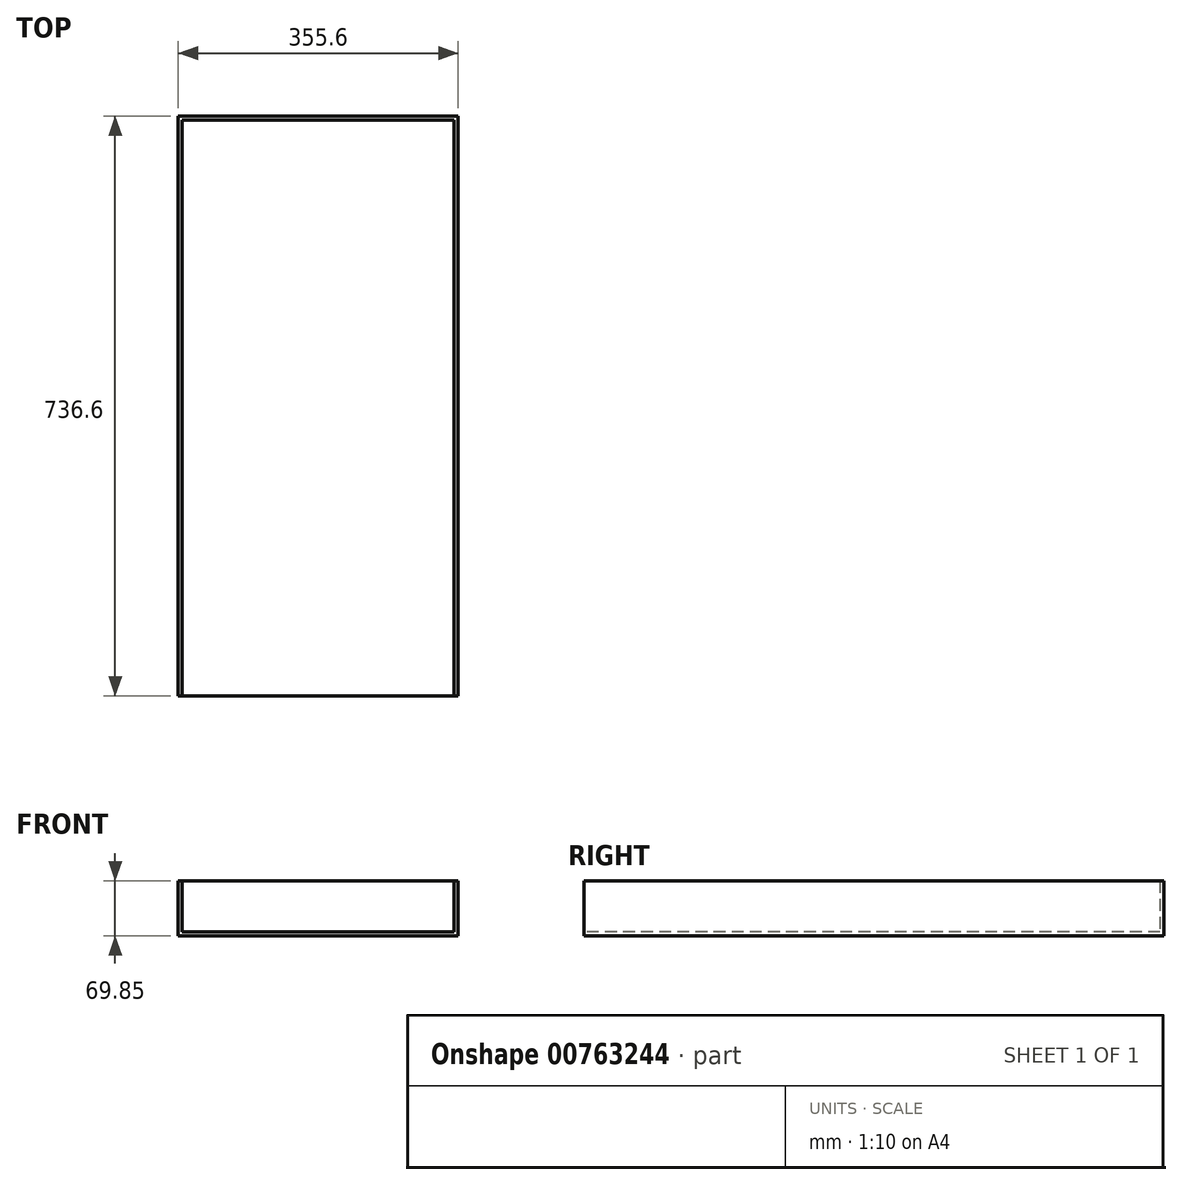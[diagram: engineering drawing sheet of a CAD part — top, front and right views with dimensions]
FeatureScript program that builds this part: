
annotation { "Feature Type Name" : "Feature", "Feature Type Description" : "" }
export const myFeature = defineFeature(function(context is Context, id is Id, definition is map)
    precondition{}
    {
        {
            var Q0;
            Q0=qCreatedBy(makeId("Front.planeOp"),FACE);
            var sketch = newSketch(context, id + "F0", { "sketchPlane" : qUnion([Q0])});
            skLineSegment(sketch, "E0", {"start": v(-177.8, 69.85) * mm, "end": v(-172.72, 69.85) * mm});
            skLineSegment(sketch, "E1", {"start": v(-172.72, 69.85) * mm, "end": v(-172.72, 5.08) * mm});
            skLineSegment(sketch, "E2", {"start": v(-172.72, 5.08) * mm, "end": v(172.72, 5.08) * mm});
            skLineSegment(sketch, "E3", {"start": v(172.72, 5.08) * mm, "end": v(172.72, 69.85) * mm});
            skLineSegment(sketch, "E4", {"start": v(172.72, 69.85) * mm, "end": v(177.8, 69.85) * mm});
            skLineSegment(sketch, "E5", {"start": v(177.8, 69.85) * mm, "end": v(177.8, 0) * mm});
            skLineSegment(sketch, "E6", {"start": v(177.8, 0) * mm, "end": v(-177.8, 0) * mm});
            skLineSegment(sketch, "E7", {"start": v(-177.8, 0) * mm, "end": v(-177.8, 69.85) * mm});
            skSolve(sketch);
        }
        {
            var Q0;
            Q0 = qSketchRegion(id + "F0", true);
            extrude(context, id + "F1", {"entities" : qUnion([Q0]), "oppositeDirection" : true, "depth" : 736.6 * mm, "offsetDistance" : 25.4 * mm});
        }
        {
            var Q0;
            Q0=makeQuery(id+"F1.opExtrude","SWEPT_FACE",FACE,{"disambiguationData":[OSD([sQuery(id+"F0.wireOp",EDGE,"E2")])]});
            var sketch = newSketch(context, id + "F2", { "sketchPlane" : qUnion([Q0])});
            skLineSegment(sketch, "E8.bottom", {"start": v(-172.72, 736.6) * mm, "end": v(172.72, 736.6) * mm});
            skLineSegment(sketch, "E8.top", {"start": v(-172.72, 731.52) * mm, "end": v(172.72, 731.52) * mm});
            skLineSegment(sketch, "E8.left", {"start": v(-172.72, 736.6) * mm, "end": v(-172.72, 731.52) * mm});
            skLineSegment(sketch, "E8.right", {"start": v(172.72, 736.6) * mm, "end": v(172.72, 731.52) * mm});
            skSolve(sketch);
        }
        {
            var Q0;
            Q0 = qSketchRegion(id + "F2", true);
            var Q1;
            Q1=makeQuery(id+"F1.opExtrude","SWEPT_FACE",FACE,{"disambiguationData":[OSD([sQuery(id+"F0.wireOp",EDGE,"E0")])]});
            extrude(context, id + "F3", {"entities" : qUnion([Q0]), "operationType" : NewBodyOperationType.ADD, "endBound" : BoundingType.UP_TO_SURFACE, "depth" : 25.4 * mm, "endBoundEntityFace" : qUnion([Q1]), "offsetDistance" : 25.4 * mm});
        }
    });
